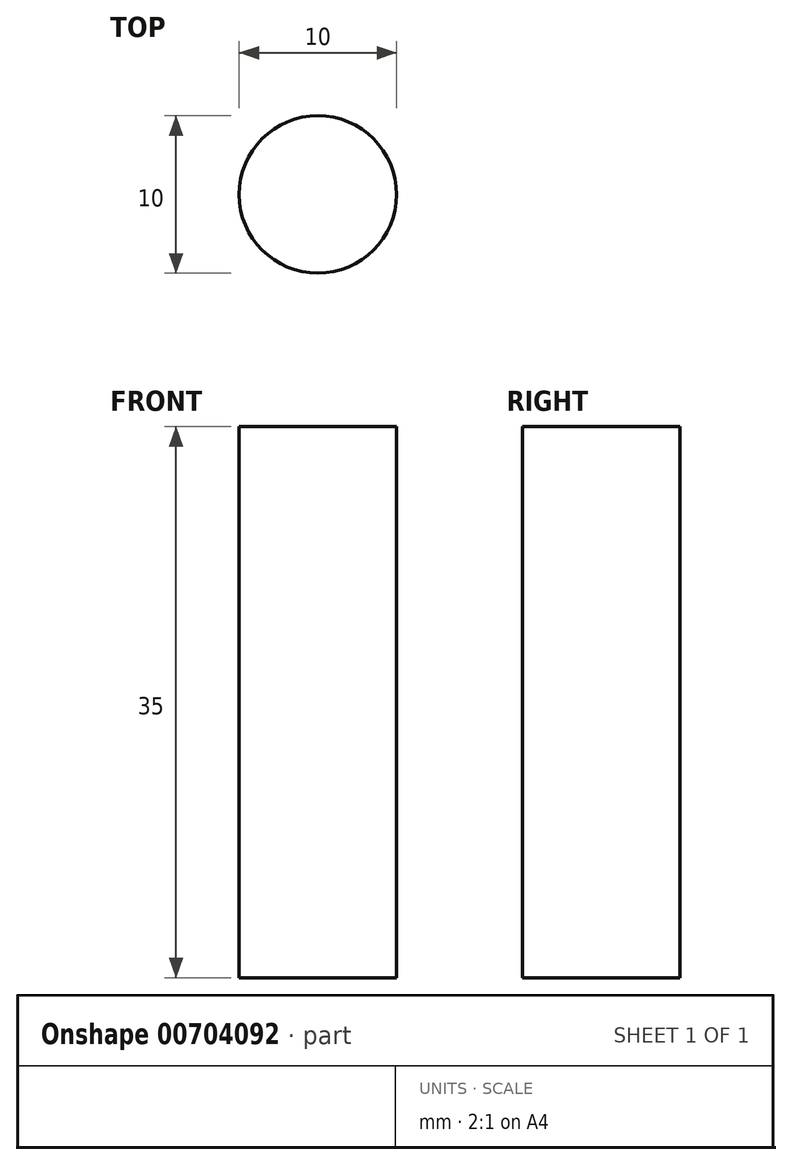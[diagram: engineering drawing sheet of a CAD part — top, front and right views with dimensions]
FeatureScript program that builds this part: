
annotation { "Feature Type Name" : "Feature", "Feature Type Description" : "" }
export const myFeature = defineFeature(function(context is Context, id is Id, definition is map)
    precondition{}
    {
        {
            var Q0;
            Q0=qCreatedBy(makeId("Top.planeOp"),FACE);
            var sketch = newSketch(context, id + "F0", { "sketchPlane" : qUnion([Q0])});
            skCircle(sketch, "E0", {"center": v(0, 0) * mm, "radius": 5 * mm});
            skSolve(sketch);
        }
        {
            var Q0;
            Q0=qSketchRegion(id+"F0",true);
            extrude(context, id + "F1", {"entities" : qUnion([Q0]), "depth" : 35 * mm});
        }
    });
